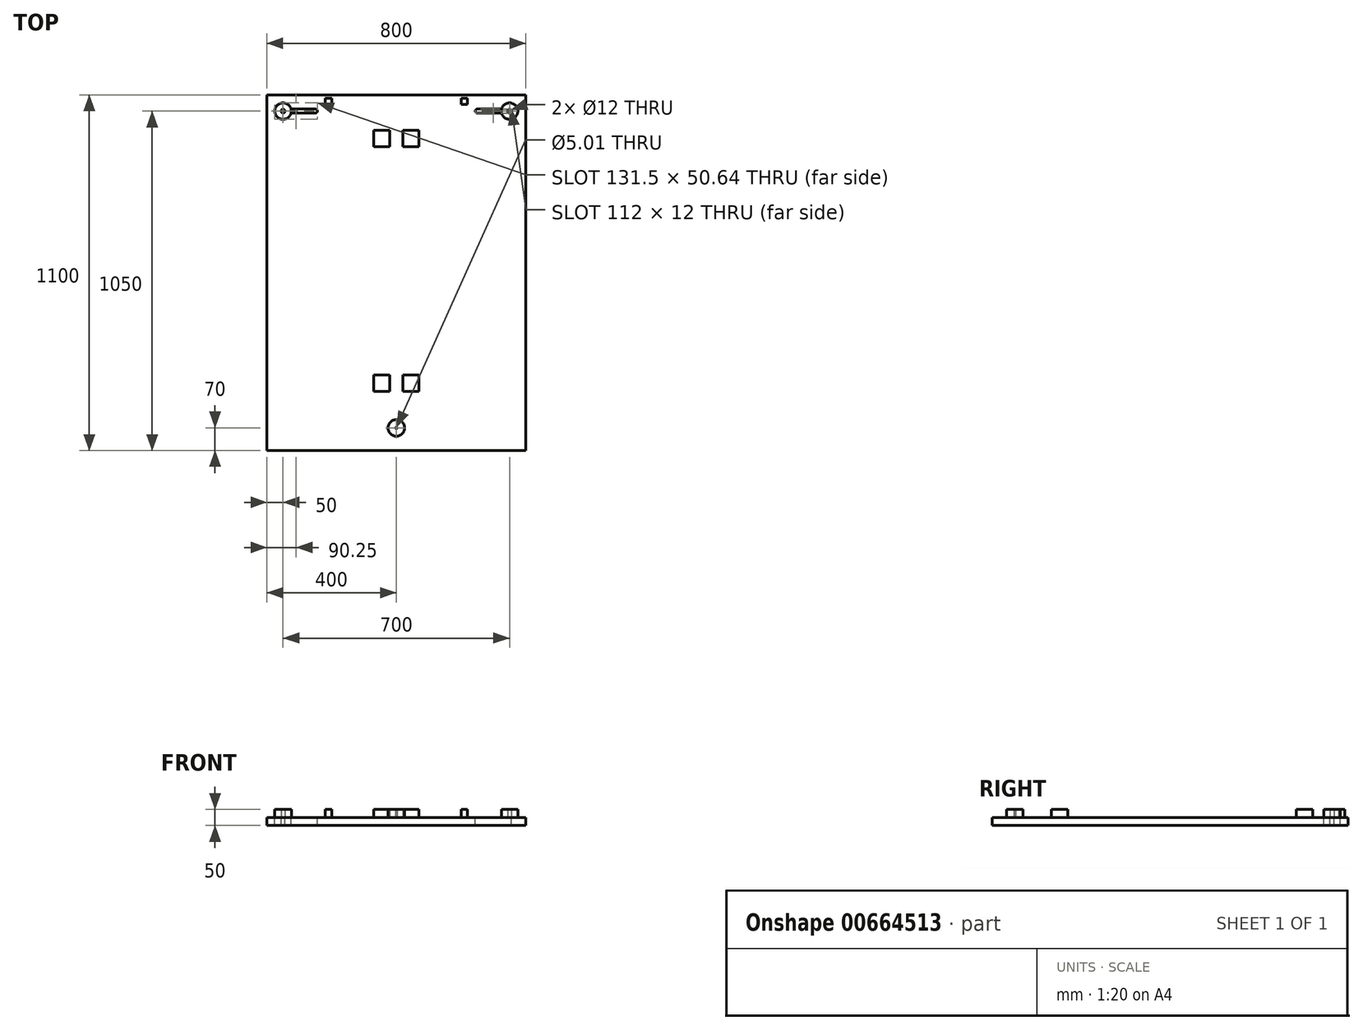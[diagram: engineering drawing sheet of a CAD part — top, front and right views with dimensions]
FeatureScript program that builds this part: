
annotation { "Feature Type Name" : "Feature", "Feature Type Description" : "" }
export const myFeature = defineFeature(function(context is Context, id is Id, definition is map)
    precondition{}
    {
        {
            var Q0;
            Q0=qCreatedBy(makeId("Top.planeOp"),FACE);
            var sketch = newSketch(context, id + "F0", { "sketchPlane" : qUnion([Q0])});
            skLineSegment(sketch, "E0.bottom", {"start": v(400, -550) * mm, "end": v(-400, -550) * mm});
            skLineSegment(sketch, "E0.top", {"start": v(400, 550) * mm, "end": v(-400, 550) * mm});
            skLineSegment(sketch, "E0.left", {"start": v(400, -550) * mm, "end": v(400, 550) * mm});
            skLineSegment(sketch, "E0.right", {"start": v(-400, -550) * mm, "end": v(-400, 550) * mm});
            skPoint(sketch, "E0.middle", {"position": v(0, 0) * mm});
            skSolve(sketch);
        }
        {
            var Q0;
            Q0 = qSketchRegion(id + "F0", true);
            extrude(context, id + "F1", {"entities" : qUnion([Q0]), "depth" : 25 * mm, "offsetDistance" : 25 * mm});
        }
        {
            var Q0;
            Q0=makeQuery(id+"F1.opExtrude","CAP_FACE",FACE,{"disambiguationData":[OSD([sQuery(id+"F0.wireOp",EDGE,"E0.bottom"),sQuery(id+"F0.wireOp",EDGE,"E0.top"),sQuery(id+"F0.wireOp",EDGE,"E0.left"),sQuery(id+"F0.wireOp",EDGE,"E0.right")])],"isStart":false});
            var sketch = newSketch(context, id + "F2", { "sketchPlane" : qUnion([Q0])});
            skLineSegment(sketch, "E1", {"start": v(0, 0) * mm, "end": v(0, -480) * mm});
            skLineSegment(sketch, "E2", {"start": v(0, 0) * mm, "end": v(0, 500) * mm});
            skLineSegment(sketch, "E3", {"start": v(0, 500) * mm, "end": v(350, 500) * mm});
            skLineSegment(sketch, "E4", {"start": v(0, 500) * mm, "end": v(-350, 500) * mm});
            skCircle(sketch, "E5", {"center": v(350, 500) * mm, "radius": 25.5 * mm});
            skCircle(sketch, "E6", {"center": v(-350, 500) * mm, "radius": 25.5 * mm});
            skCircle(sketch, "E7", {"center": v(0, -480) * mm, "radius": 2.5 * mm});
            skCircle(sketch, "E8", {"center": v(0, -480) * mm, "radius": 25.5 * mm});
            skLineSegment(sketch, "E9", {"start": v(-102.98, 500) * mm, "end": v(-102.98, 440) * mm});
            skLineSegment(sketch, "E10", {"start": v(0, 440) * mm, "end": v(-20, 440) * mm});
            skLineSegment(sketch, "E11.bottom", {"start": v(-20, 440) * mm, "end": v(-70, 440) * mm});
            skLineSegment(sketch, "E11.top", {"start": v(-20, 390) * mm, "end": v(-70, 390) * mm});
            skLineSegment(sketch, "E11.left", {"start": v(-20, 440) * mm, "end": v(-20, 390) * mm});
            skLineSegment(sketch, "E11.right", {"start": v(-70, 440) * mm, "end": v(-70, 390) * mm});
            skLineSegment(sketch, "E12.MirrorCS", {"start": v(20, 440) * mm, "end": v(20, 390) * mm});
            skLineSegment(sketch, "E13.MirrorCS", {"start": v(20, 440) * mm, "end": v(70, 440) * mm});
            skLineSegment(sketch, "E14.MirrorCS", {"start": v(70, 440) * mm, "end": v(70, 390) * mm});
            skLineSegment(sketch, "E15.MirrorCS", {"start": v(20, 390) * mm, "end": v(70, 390) * mm});
            skLineSegment(sketch, "E16", {"start": v(0, 36.65) * mm, "end": v(-124.44, 36.65) * mm});
            skLineSegment(sketch, "E17.MirrorCS", {"start": v(-20, -366.7) * mm, "end": v(-70, -366.7) * mm});
            skLineSegment(sketch, "E18.MirrorCS", {"start": v(-20, -316.7) * mm, "end": v(-70, -316.7) * mm});
            skLineSegment(sketch, "E19.MirrorCS", {"start": v(-70, -366.7) * mm, "end": v(-70, -316.7) * mm});
            skLineSegment(sketch, "E20.MirrorCS", {"start": v(-20, -366.7) * mm, "end": v(-20, -316.7) * mm});
            skLineSegment(sketch, "E21.MirrorCS", {"start": v(20, -366.7) * mm, "end": v(70, -366.7) * mm});
            skLineSegment(sketch, "E22.MirrorCS", {"start": v(20, -366.7) * mm, "end": v(20, -316.7) * mm});
            skLineSegment(sketch, "E23.MirrorCS", {"start": v(20, -316.7) * mm, "end": v(70, -316.7) * mm});
            skLineSegment(sketch, "E24.MirrorCS", {"start": v(70, -366.7) * mm, "end": v(70, -316.7) * mm});
            skLineSegment(sketch, "E25", {"start": v(0, 500) * mm, "end": v(0, 520) * mm});
            skLineSegment(sketch, "E26", {"start": v(0, 520) * mm, "end": v(-200, 520) * mm});
            skLineSegment(sketch, "E27.bottom", {"start": v(-200, 520) * mm, "end": v(-220, 520) * mm});
            skLineSegment(sketch, "E27.top", {"start": v(-200, 540) * mm, "end": v(-220, 540) * mm});
            skLineSegment(sketch, "E27.left", {"start": v(-200, 520) * mm, "end": v(-200, 540) * mm});
            skLineSegment(sketch, "E27.right", {"start": v(-220, 520) * mm, "end": v(-220, 540) * mm});
            skLineSegment(sketch, "E28.MirrorCS", {"start": v(200, 520) * mm, "end": v(200, 540) * mm});
            skLineSegment(sketch, "E29.MirrorCS", {"start": v(220, 520) * mm, "end": v(220, 540) * mm});
            skLineSegment(sketch, "E30.MirrorCS", {"start": v(200, 520) * mm, "end": v(220, 520) * mm});
            skLineSegment(sketch, "E31.MirrorCS", {"start": v(200, 540) * mm, "end": v(220, 540) * mm});
            skCircle(sketch, "E32", {"center": v(350, 500) * mm, "radius": 6 * mm});
            skLineSegment(sketch, "E33", {"start": v(350, 500) * mm, "end": v(350, 441.27) * mm});
            skLineSegment(sketch, "E34", {"start": v(350, 441.27) * mm, "end": v(250, 441.27) * mm});
            skCircle(sketch, "E35", {"center": v(250, 500) * mm, "radius": 6 * mm});
            skLineSegment(sketch, "E36", {"start": v(250, 494) * mm, "end": v(350, 494) * mm});
            skLineSegment(sketch, "E37", {"start": v(250, 506) * mm, "end": v(350, 506) * mm});
            skLineSegment(sketch, "E38.MirrorCS", {"start": v(-250, 506) * mm, "end": v(-350, 506) * mm});
            skLineSegment(sketch, "E39.MirrorCS", {"start": v(-250, 494) * mm, "end": v(-350, 494) * mm});
            skCircle(sketch, "E40.MirrorC", {"center": v(-350, 500) * mm, "radius": 6 * mm});
            skCircle(sketch, "E41.MirrorC", {"center": v(-250, 500) * mm, "radius": 6 * mm});
            skSolve(sketch);
        }
        {
            var Q0;
            {var subQ0=sQuery(id+"F2.wireOp",EDGE,"E41.MirrorC");var subQ1=sQuery(id+"F2.wireOp",EDGE,"E4");var subQ2=makeQuery(id+"F2.imprint","INTERSECT",VERTEX,{"disambiguationData":[OD(0.0)],"derivedFrom":[subQ1,subQ0]});Q0=makeQuery(id+"F2.imprint","IMPRINT",FACE,{"disambiguationData":[TD([[makeQuery(id+"F2.imprint","IMPRINT",EDGE,{"disambiguationData":[TD([[subQ2,-1.0]])],"derivedFrom":subQ1}),-1.0]])]});}
            var Q1;
            {var subQ0=sQuery(id+"F2.wireOp",EDGE,"E41.MirrorC");var subQ1=sQuery(id+"F2.wireOp",EDGE,"E4");var subQ2=makeQuery(id+"F2.imprint","INTERSECT",VERTEX,{"disambiguationData":[OD(0.0)],"derivedFrom":[subQ1,subQ0]});Q1=makeQuery(id+"F2.imprint","IMPRINT",FACE,{"disambiguationData":[TD([[makeQuery(id+"F2.imprint","IMPRINT",EDGE,{"disambiguationData":[TD([[subQ2,-1.0]])],"derivedFrom":subQ1}),1.0]])]});}
            var Q2;
            {var subQ0=sQuery(id+"F2.wireOp",EDGE,"E41.MirrorC");var subQ1=sQuery(id+"F2.wireOp",EDGE,"E4");var subQ2=makeQuery(id+"F2.imprint","INTERSECT",VERTEX,{"disambiguationData":[OD(1.0)],"derivedFrom":[subQ1,subQ0]});Q2=makeQuery(id+"F2.imprint","IMPRINT",FACE,{"disambiguationData":[TD([[makeQuery(id+"F2.imprint","IMPRINT",EDGE,{"disambiguationData":[TD([[subQ2,-1.0]])],"derivedFrom":subQ1}),1.0]])]});}
            var Q3;
            {var subQ0=sQuery(id+"F2.wireOp",EDGE,"E41.MirrorC");var subQ1=sQuery(id+"F2.wireOp",EDGE,"E4");var subQ2=makeQuery(id+"F2.imprint","INTERSECT",VERTEX,{"disambiguationData":[OD(1.0)],"derivedFrom":[subQ1,subQ0]});Q3=makeQuery(id+"F2.imprint","IMPRINT",FACE,{"disambiguationData":[TD([[makeQuery(id+"F2.imprint","IMPRINT",EDGE,{"disambiguationData":[TD([[subQ2,-1.0]])],"derivedFrom":subQ1}),-1.0]])]});}
            var Q4;
            {var subQ0=sQuery(id+"F2.wireOp",EDGE,"E40.MirrorC");var subQ1=makeQuery(id+"F2.imprint","INTERSECT",VERTEX,{"derivedFrom":[sQuery(id+"F2.wireOp",EDGE,"E38.MirrorCS"),subQ0]});Q4=makeQuery(id+"F2.imprint","IMPRINT",FACE,{"disambiguationData":[TD([[makeQuery(id+"F2.imprint","IMPRINT",EDGE,{"disambiguationData":[TD([[subQ1,-1.0]])],"derivedFrom":subQ0}),-1.0]])]});}
            var Q5;
            {var subQ0=sQuery(id+"F2.wireOp",EDGE,"E40.MirrorC");var subQ1=sQuery(id+"F2.wireOp",EDGE,"E4");var subQ2=makeQuery(id+"F2.imprint","INTERSECT",VERTEX,{"derivedFrom":[subQ1,subQ0]});Q5=makeQuery(id+"F2.imprint","IMPRINT",FACE,{"disambiguationData":[TD([[makeQuery(id+"F2.imprint","IMPRINT",EDGE,{"disambiguationData":[TD([[subQ2,1.0]])],"derivedFrom":subQ1}),1.0]])]});}
            var Q6;
            {var subQ0=sQuery(id+"F2.wireOp",EDGE,"E40.MirrorC");var subQ1=sQuery(id+"F2.wireOp",EDGE,"E4");var subQ2=makeQuery(id+"F2.imprint","INTERSECT",VERTEX,{"derivedFrom":[subQ1,subQ0]});Q6=makeQuery(id+"F2.imprint","IMPRINT",FACE,{"disambiguationData":[TD([[makeQuery(id+"F2.imprint","IMPRINT",EDGE,{"disambiguationData":[TD([[subQ2,1.0]])],"derivedFrom":subQ1}),-1.0]])]});}
            var Q7;
            {var subQ0=sQuery(id+"F2.wireOp",EDGE,"E35");var subQ1=sQuery(id+"F2.wireOp",EDGE,"E3");var subQ2=makeQuery(id+"F2.imprint","INTERSECT",VERTEX,{"disambiguationData":[OD(1.0)],"derivedFrom":[subQ1,subQ0]});Q7=makeQuery(id+"F2.imprint","IMPRINT",FACE,{"disambiguationData":[TD([[makeQuery(id+"F2.imprint","IMPRINT",EDGE,{"disambiguationData":[TD([[subQ2,-1.0]])],"derivedFrom":subQ1}),1.0]])]});}
            var Q8;
            {var subQ0=sQuery(id+"F2.wireOp",EDGE,"E35");var subQ1=sQuery(id+"F2.wireOp",EDGE,"E3");var subQ2=makeQuery(id+"F2.imprint","INTERSECT",VERTEX,{"disambiguationData":[OD(1.0)],"derivedFrom":[subQ1,subQ0]});Q8=makeQuery(id+"F2.imprint","IMPRINT",FACE,{"disambiguationData":[TD([[makeQuery(id+"F2.imprint","IMPRINT",EDGE,{"disambiguationData":[TD([[subQ2,-1.0]])],"derivedFrom":subQ1}),-1.0]])]});}
            var Q9;
            {var subQ0=sQuery(id+"F2.wireOp",EDGE,"E5");var subQ1=sQuery(id+"F2.wireOp",EDGE,"E3");var subQ2=makeQuery(id+"F2.imprint","INTERSECT",VERTEX,{"derivedFrom":[subQ1,subQ0]});Q9=makeQuery(id+"F2.imprint","IMPRINT",FACE,{"disambiguationData":[TD([[makeQuery(id+"F2.imprint","IMPRINT",EDGE,{"disambiguationData":[TD([[subQ2,-1.0]])],"derivedFrom":subQ1}),1.0]])]});}
            var Q10;
            {var subQ0=sQuery(id+"F2.wireOp",EDGE,"E5");var subQ1=sQuery(id+"F2.wireOp",EDGE,"E3");var subQ2=makeQuery(id+"F2.imprint","INTERSECT",VERTEX,{"derivedFrom":[subQ1,subQ0]});Q10=makeQuery(id+"F2.imprint","IMPRINT",FACE,{"disambiguationData":[TD([[makeQuery(id+"F2.imprint","IMPRINT",EDGE,{"disambiguationData":[TD([[subQ2,-1.0]])],"derivedFrom":subQ1}),-1.0]])]});}
            var Q11;
            {var subQ0=sQuery(id+"F2.wireOp",EDGE,"E33");var subQ1=sQuery(id+"F2.wireOp",EDGE,"E3");var subQ2=makeQuery(id+"F2.imprint","INTERSECT",VERTEX,{"derivedFrom":[subQ1,subQ0]});Q11=makeQuery(id+"F2.imprint","IMPRINT",FACE,{"disambiguationData":[TD([[makeQuery(id+"F2.imprint","IMPRINT",EDGE,{"disambiguationData":[TD([[subQ2,1.0]])],"derivedFrom":subQ1}),1.0]])]});}
            var Q12;
            {var subQ0=sQuery(id+"F2.wireOp",EDGE,"E33");var subQ1=sQuery(id+"F2.wireOp",EDGE,"E3");var subQ2=makeQuery(id+"F2.imprint","INTERSECT",VERTEX,{"derivedFrom":[subQ1,subQ0]});Q12=makeQuery(id+"F2.imprint","IMPRINT",FACE,{"disambiguationData":[TD([[makeQuery(id+"F2.imprint","IMPRINT",EDGE,{"disambiguationData":[TD([[subQ2,1.0]])],"derivedFrom":subQ1}),-1.0]])]});}
            var Q13;
            {var subQ0=sQuery(id+"F2.wireOp",EDGE,"E35");var subQ1=sQuery(id+"F2.wireOp",EDGE,"E3");var subQ2=makeQuery(id+"F2.imprint","INTERSECT",VERTEX,{"disambiguationData":[OD(0.0)],"derivedFrom":[subQ1,subQ0]});Q13=makeQuery(id+"F2.imprint","IMPRINT",FACE,{"disambiguationData":[TD([[makeQuery(id+"F2.imprint","IMPRINT",EDGE,{"disambiguationData":[TD([[subQ2,-1.0]])],"derivedFrom":subQ1}),1.0]])]});}
            var Q14;
            {var subQ0=sQuery(id+"F2.wireOp",EDGE,"E35");var subQ1=sQuery(id+"F2.wireOp",EDGE,"E3");var subQ2=makeQuery(id+"F2.imprint","INTERSECT",VERTEX,{"disambiguationData":[OD(0.0)],"derivedFrom":[subQ1,subQ0]});Q14=makeQuery(id+"F2.imprint","IMPRINT",FACE,{"disambiguationData":[TD([[makeQuery(id+"F2.imprint","IMPRINT",EDGE,{"disambiguationData":[TD([[subQ2,-1.0]])],"derivedFrom":subQ1}),-1.0]])]});}
            extrude(context, id + "F3", {"entities" : qUnion([Q0, Q1, Q2, Q3, Q4, Q5, Q6, Q7, Q8, Q9, Q10, Q11, Q12, Q13, Q14]), "operationType" : NewBodyOperationType.REMOVE, "oppositeDirection" : true, "depth" : 25 * mm, "offsetDistance" : 25 * mm});
        }
        {
            var Q0;
            Q0=makeQuery(id+"F2.imprint","IMPRINT",FACE,{"disambiguationData":[TD([[makeQuery(id+"F2.imprint","IMPRINT",EDGE,{"derivedFrom":sQuery(id+"F2.wireOp",EDGE,"E7")}),-1.0]])]});
            var Q1;
            Q1=makeQuery(id+"F2.imprint","IMPRINT",FACE,{"disambiguationData":[TD([[makeQuery(id+"F2.imprint","IMPRINT",EDGE,{"derivedFrom":sQuery(id+"F2.wireOp",EDGE,"E21.MirrorCS")}),1.0]])]});
            var Q2;
            Q2=makeQuery(id+"F2.imprint","IMPRINT",FACE,{"disambiguationData":[TD([[makeQuery(id+"F2.imprint","IMPRINT",EDGE,{"derivedFrom":sQuery(id+"F2.wireOp",EDGE,"E17.MirrorCS")}),-1.0]])]});
            var Q3;
            Q3=makeQuery(id+"F2.imprint","IMPRINT",FACE,{"disambiguationData":[TD([[makeQuery(id+"F2.imprint","IMPRINT",EDGE,{"derivedFrom":sQuery(id+"F2.wireOp",EDGE,"E11.bottom")}),1.0]])]});
            var Q4;
            Q4=makeQuery(id+"F2.imprint","IMPRINT",FACE,{"disambiguationData":[TD([[makeQuery(id+"F2.imprint","IMPRINT",EDGE,{"derivedFrom":sQuery(id+"F2.wireOp",EDGE,"E12.MirrorCS")}),1.0]])]});
            var Q5;
            Q5=makeQuery(id+"F2.imprint","IMPRINT",FACE,{"disambiguationData":[TD([[makeQuery(id+"F2.imprint","IMPRINT",EDGE,{"derivedFrom":sQuery(id+"F2.wireOp",EDGE,"E28.MirrorCS")}),-1.0]])]});
            var Q6;
            Q6=makeQuery(id+"F2.imprint","IMPRINT",FACE,{"disambiguationData":[TD([[makeQuery(id+"F2.imprint","IMPRINT",EDGE,{"derivedFrom":sQuery(id+"F2.wireOp",EDGE,"E27.bottom")}),-1.0]])]});
            var Q7;
            {var subQ0=sQuery(id+"F2.wireOp",EDGE,"E38.MirrorCS");var subQ1=sQuery(id+"F2.wireOp",EDGE,"E6");var subQ2=makeQuery(id+"F2.imprint","INTERSECT",VERTEX,{"derivedFrom":[subQ1,subQ0]});Q7=makeQuery(id+"F2.imprint","IMPRINT",FACE,{"disambiguationData":[TD([[makeQuery(id+"F2.imprint","IMPRINT",EDGE,{"disambiguationData":[TD([[subQ2,-1.0]])],"derivedFrom":subQ1}),1.0]])]});}
            var Q8;
            {var subQ0=sQuery(id+"F2.wireOp",EDGE,"E40.MirrorC");var subQ1=sQuery(id+"F2.wireOp",EDGE,"E4");var subQ2=makeQuery(id+"F2.imprint","INTERSECT",VERTEX,{"derivedFrom":[subQ1,subQ0]});Q8=makeQuery(id+"F2.imprint","IMPRINT",FACE,{"disambiguationData":[TD([[makeQuery(id+"F2.imprint","IMPRINT",EDGE,{"disambiguationData":[TD([[subQ2,1.0]])],"derivedFrom":subQ1}),-1.0]])]});}
            var Q9;
            {var subQ0=sQuery(id+"F2.wireOp",EDGE,"E40.MirrorC");var subQ1=sQuery(id+"F2.wireOp",EDGE,"E4");var subQ2=makeQuery(id+"F2.imprint","INTERSECT",VERTEX,{"derivedFrom":[subQ1,subQ0]});Q9=makeQuery(id+"F2.imprint","IMPRINT",FACE,{"disambiguationData":[TD([[makeQuery(id+"F2.imprint","IMPRINT",EDGE,{"disambiguationData":[TD([[subQ2,1.0]])],"derivedFrom":subQ1}),1.0]])]});}
            var Q10;
            {var subQ0=sQuery(id+"F2.wireOp",EDGE,"E33");var subQ1=sQuery(id+"F2.wireOp",EDGE,"E5");var subQ2=makeQuery(id+"F2.imprint","INTERSECT",VERTEX,{"derivedFrom":[subQ1,subQ0]});Q10=makeQuery(id+"F2.imprint","IMPRINT",FACE,{"disambiguationData":[TD([[makeQuery(id+"F2.imprint","IMPRINT",EDGE,{"disambiguationData":[TD([[subQ2,-1.0]])],"derivedFrom":subQ1}),1.0]])]});}
            var Q11;
            {var subQ0=sQuery(id+"F2.wireOp",EDGE,"E33");var subQ1=sQuery(id+"F2.wireOp",EDGE,"E5");var subQ2=makeQuery(id+"F2.imprint","INTERSECT",VERTEX,{"derivedFrom":[subQ1,subQ0]});Q11=makeQuery(id+"F2.imprint","IMPRINT",FACE,{"disambiguationData":[TD([[makeQuery(id+"F2.imprint","IMPRINT",EDGE,{"disambiguationData":[TD([[subQ2,1.0]])],"derivedFrom":subQ1}),1.0]])]});}
            var Q12;
            {var subQ0=sQuery(id+"F2.wireOp",EDGE,"E5");var subQ1=sQuery(id+"F2.wireOp",EDGE,"E3");var subQ2=makeQuery(id+"F2.imprint","INTERSECT",VERTEX,{"derivedFrom":[subQ1,subQ0]});Q12=makeQuery(id+"F2.imprint","IMPRINT",FACE,{"disambiguationData":[TD([[makeQuery(id+"F2.imprint","IMPRINT",EDGE,{"disambiguationData":[TD([[subQ2,-1.0]])],"derivedFrom":subQ1}),1.0]])]});}
            var Q13;
            {var subQ0=sQuery(id+"F2.wireOp",EDGE,"E5");var subQ1=sQuery(id+"F2.wireOp",EDGE,"E3");var subQ2=makeQuery(id+"F2.imprint","INTERSECT",VERTEX,{"derivedFrom":[subQ1,subQ0]});Q13=makeQuery(id+"F2.imprint","IMPRINT",FACE,{"disambiguationData":[TD([[makeQuery(id+"F2.imprint","IMPRINT",EDGE,{"disambiguationData":[TD([[subQ2,-1.0]])],"derivedFrom":subQ1}),-1.0]])]});}
            extrude(context, id + "F4", {"entities" : qUnion([Q0, Q1, Q2, Q3, Q4, Q5, Q6, Q7, Q8, Q9, Q10, Q11, Q12, Q13]), "depth" : 25 * mm, "offsetDistance" : 25 * mm});
        }
    });
